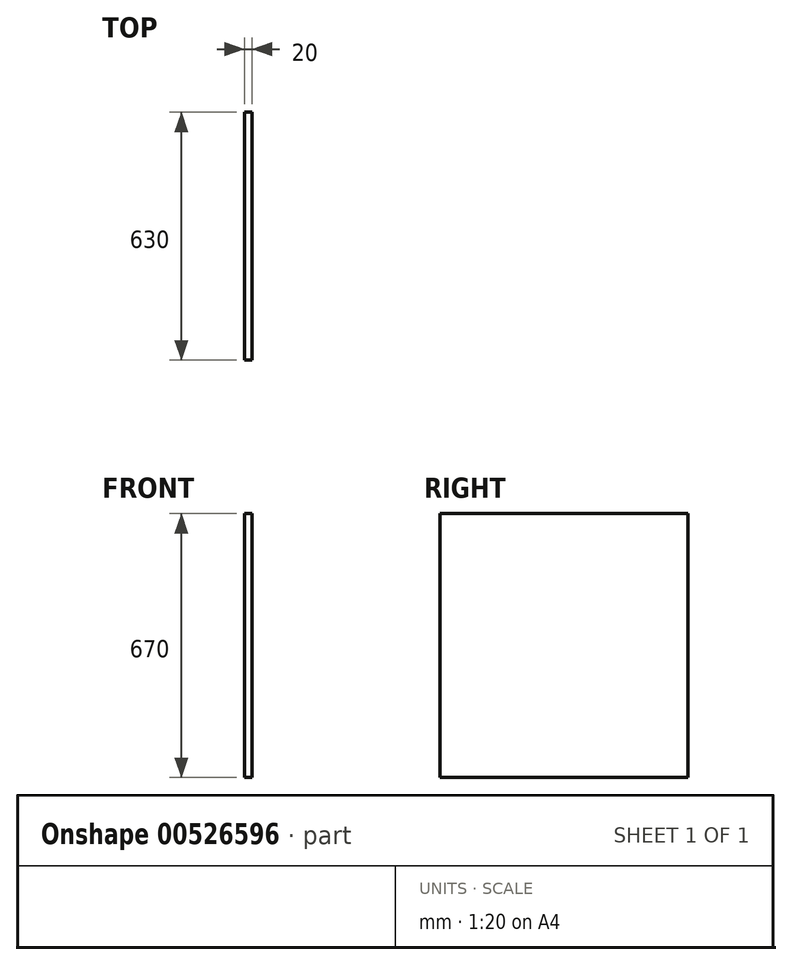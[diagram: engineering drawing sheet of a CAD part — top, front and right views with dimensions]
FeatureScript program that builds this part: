
annotation { "Feature Type Name" : "Feature", "Feature Type Description" : "" }
export const myFeature = defineFeature(function(context is Context, id is Id, definition is map)
    precondition{}
    {
        {
            var Q0;
            Q0=qCreatedBy(makeId("Right.planeOp"),FACE);
            var sketch = newSketch(context, id + "F0", { "sketchPlane" : qUnion([Q0])});
            skLineSegment(sketch, "E0.bottom", {"start": v(315, 335) * mm, "end": v(-315, 335) * mm});
            skLineSegment(sketch, "E0.top", {"start": v(315, -335) * mm, "end": v(-315, -335) * mm});
            skLineSegment(sketch, "E0.left", {"start": v(315, 335) * mm, "end": v(315, -335) * mm});
            skLineSegment(sketch, "E0.right", {"start": v(-315, 335) * mm, "end": v(-315, -335) * mm});
            skPoint(sketch, "E0.middle", {"position": v(0, 0) * mm});
            skSolve(sketch);
        }
        {
            var Q0;
            Q0=makeQuery(id+"F0.imprint","IMPRINT",FACE,{"disambiguationData":[TD([[makeQuery(id+"F0.imprint","IMPRINT",EDGE,{"derivedFrom":sQuery(id+"F0.wireOp",EDGE,"E0.bottom")}),1.0]])]});
            extrude(context, id + "F1", {"entities" : qUnion([Q0]), "depth" : 20 * mm, "offsetDistance" : 25 * mm});
        }
    });
